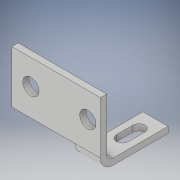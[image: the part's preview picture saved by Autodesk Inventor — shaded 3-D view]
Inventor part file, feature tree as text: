
AUTODESK INVENTOR PART (.ipt)
format: ipt  version: 2017 (Build 210142000, 142)  size: 180,736 bytes
history: native  units: in
note: dims shown in document units (in); Inventor stores cm internally (conversion verified against a paired STEP export)
features: sketch x5, extrude x4, other x1
ambient origin geometry x8: Origin, YZ Plane, XZ Plane, XY Plane, X Axis, Y Axis, Z Axis, Center Point
bodies: Solid1 (feature_tree)
feature tree (10):
  extrude  "Extrusion1"  Depth=0.496in
  extrude  "Extrusion2"  Depth=0.238in
  extrude  "Extrusion4"  Depth=0.059in
  extrude  "Extrusion5"  Depth=0.238in
  other  "Bend Part3"
  sketch  "Sketch1"  dims[d0=0.838in d1=0.496in]
  sketch  "Sketch2"  dims[d2=0.238in d3=0.615in]
  sketch  "Sketch3"  dims[d4=0.059in d5=0.0in d6=0.154in]
  sketch  "Sketch6"  dims[d7=0.238in d8=0.18in]
  sketch  "Sketch17"  dims[d9=0.7874in d11=0.539in d12=0.3937in d14=1.0in d16=1.0in d17=0.0in d18=0.114in d19=0.157in d20=0.119in d24=0.7874in d26=0.156in d27=0.3937in d29=1.0in d31=1.0in d32=0.0in d33=1.0in d34=0.0in d53=0.059in d54=90.0deg]
